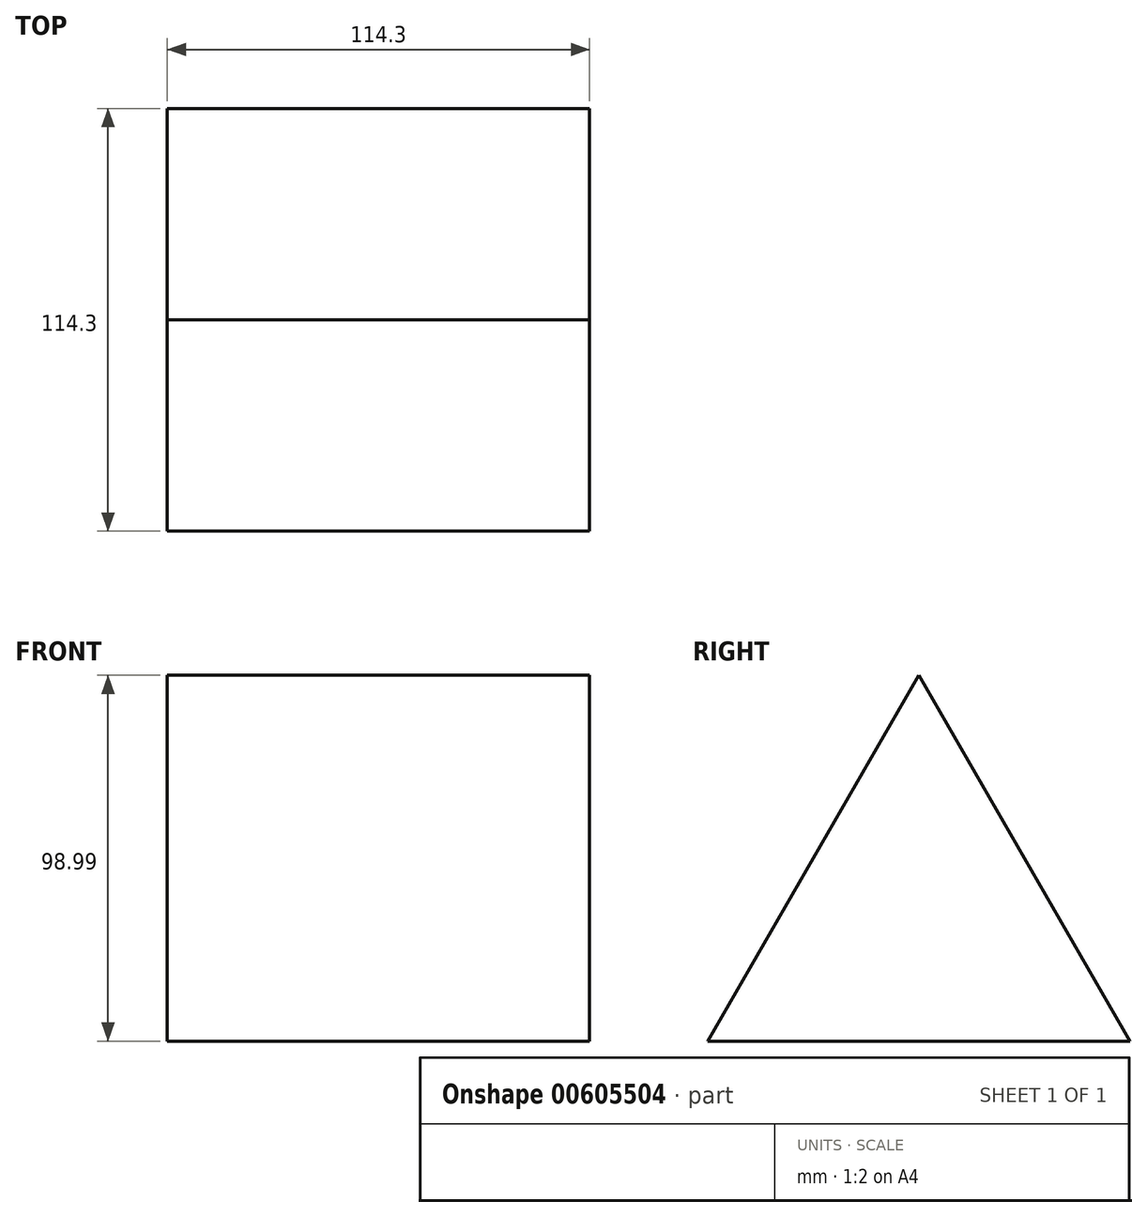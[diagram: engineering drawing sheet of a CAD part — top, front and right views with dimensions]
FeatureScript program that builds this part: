
annotation { "Feature Type Name" : "Feature", "Feature Type Description" : "" }
export const myFeature = defineFeature(function(context is Context, id is Id, definition is map)
    precondition{}
    {
        {
            var Q0;
            Q0=qCreatedBy(makeId("Right.planeOp"),FACE);
            var sketch = newSketch(context, id + "F0", { "sketchPlane" : qUnion([Q0])});
            skLineSegment(sketch, "E0", {"start": v(0, 54.7) * mm, "end": v(57.15, -44.28) * mm});
            skLineSegment(sketch, "E1", {"start": v(57.15, -44.28) * mm, "end": v(-57.15, -44.28) * mm});
            skLineSegment(sketch, "E2", {"start": v(-57.15, -44.28) * mm, "end": v(0, 54.7) * mm});
            skSolve(sketch);
        }
        {
            var Q0;
            Q0 = qSketchRegion(id + "F0", true);
            extrude(context, id + "F1", {"entities" : qUnion([Q0]), "depth" : 114.3 * mm, "offsetDistance" : 25.4 * mm});
        }
    });
